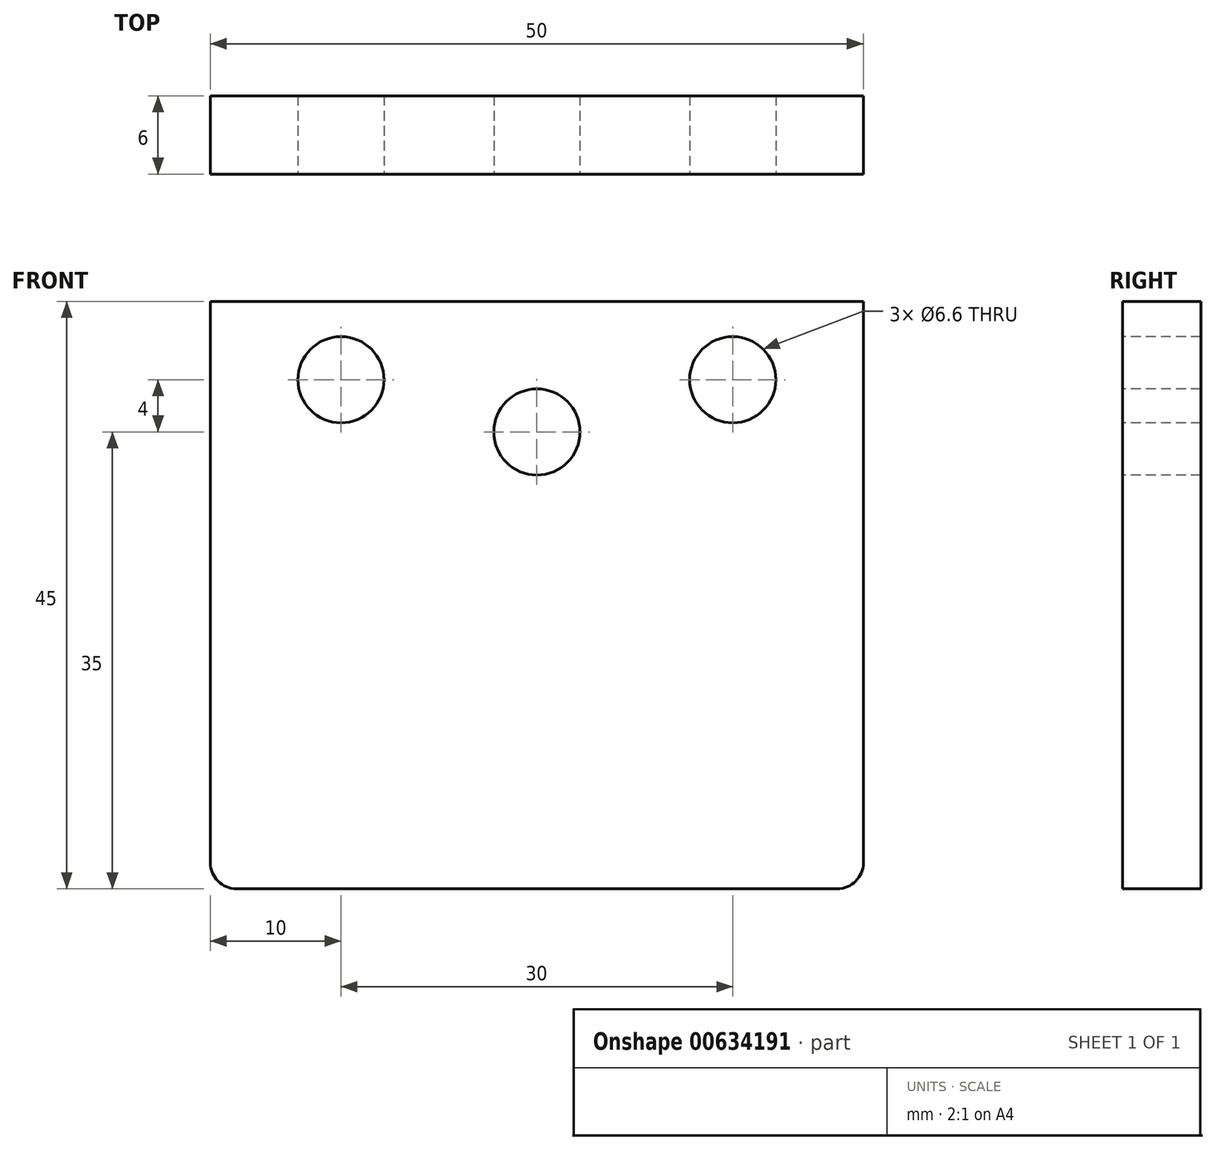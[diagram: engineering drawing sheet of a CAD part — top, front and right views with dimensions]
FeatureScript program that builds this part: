
annotation { "Feature Type Name" : "Feature", "Feature Type Description" : "" }
export const myFeature = defineFeature(function(context is Context, id is Id, definition is map)
    precondition{}
    {
        {
            var Q0;
            Q0=qCreatedBy(makeId("Front.planeOp"),FACE);
            var sketch = newSketch(context, id + "F0", { "sketchPlane" : qUnion([Q0])});
            skLineSegment(sketch, "E0.bottom", {"start": v(0, 0) * mm, "end": v(50, 0) * mm});
            skLineSegment(sketch, "E0.top", {"start": v(0, 45) * mm, "end": v(50, 45) * mm});
            skLineSegment(sketch, "E0.left", {"start": v(0, 0) * mm, "end": v(0, 45) * mm});
            skLineSegment(sketch, "E0.right", {"start": v(50, 0) * mm, "end": v(50, 45) * mm});
            skSolve(sketch);
        }
        {
            var Q0;
            Q0=makeQuery(id+"F0.imprint","IMPRINT",FACE,{"disambiguationData":[TD([[makeQuery(id+"F0.imprint","IMPRINT",EDGE,{"derivedFrom":sQuery(id+"F0.wireOp",EDGE,"E0.bottom")}),1.0]])]});
            extrude(context, id + "F1", {"entities" : qUnion([Q0]), "depth" : 6 * mm, "offsetDistance" : 25 * mm});
        }
        {
            var Q0;
            Q0=makeQuery(id+"F1.opExtrude","CAP_FACE",FACE,{"disambiguationData":[OSD([sQuery(id+"F0.wireOp",EDGE,"E0.bottom"),sQuery(id+"F0.wireOp",EDGE,"E0.top"),sQuery(id+"F0.wireOp",EDGE,"E0.left"),sQuery(id+"F0.wireOp",EDGE,"E0.right")])],"isStart":false});
            var sketch = newSketch(context, id + "F2", { "sketchPlane" : qUnion([Q0])});
            skPoint(sketch, "E1", {"position": v(10, 39) * mm});
            skPoint(sketch, "E2", {"position": v(40, 39) * mm});
            skPoint(sketch, "E3", {"position": v(25, 35) * mm});
            skPoint(sketch, "E3.positionSnap0", {"position": v(25, 45) * mm});
            skSolve(sketch);
        }
        {
            var Q0;
            Q0=sQuery(id+"F2.wireOp",VERTEX,"E1");
            var Q1;
            Q1=sQuery(id+"F2.wireOp",VERTEX,"E3");
            var Q2;
            Q2=sQuery(id+"F2.wireOp",VERTEX,"E2");
            var Q3;
            Q3=makeQuery(id+"F1.opExtrude","SWEPT_BODY",BODY,{"disambiguationData":[OSD([sQuery(id+"F0.wireOp",EDGE,"E0.bottom"),sQuery(id+"F0.wireOp",EDGE,"E0.top"),sQuery(id+"F0.wireOp",EDGE,"E0.left"),sQuery(id+"F0.wireOp",EDGE,"E0.right")])]});
            hole(context, id + "F3", {"style" : HoleStyle.SIMPLE, "endStyle" : HoleEndStyle.THROUGH, "standardTappedOrClearance" : lookupTablePath({ "standard" : "ISO", "fit" : "Normal", "size" : "M6", "type" : "Clearance" }), "standardBlindInLast" : lookupTablePath({ "fit" : "Standard", "standard" : "ISO", "size" : "M6", "type" : "Clearance" }), "holeDiameter" : 6.6 * mm, "majorDiameter" : 6 * mm, "isTappedThrough" : true, "tappedDepth" : 8 * mm, "tapClearance" : 3, "startFromSketch" : true, "locations" : qUnion([Q0, Q1, Q2]), "scope" : qUnion([Q3])});
        }
        {
            var Q0;
            Q0=makeQuery(id+"F1.opExtrude","SWEPT_EDGE",EDGE,{"disambiguationData":[OSD([sQuery(id+"F0.wireOp",EDGE,"E0.bottom"),sQuery(id+"F0.wireOp",EDGE,"E0.right")])]});
            var Q1;
            Q1=makeQuery(id+"F1.opExtrude","SWEPT_EDGE",EDGE,{"disambiguationData":[OSD([sQuery(id+"F0.wireOp",EDGE,"E0.bottom"),sQuery(id+"F0.wireOp",EDGE,"E0.left")])]});
            fillet(context, id + "F4", {"entities" : qUnion([Q0, Q1]), "radius" : 2 * mm, "tangentPropagation" : true, "allowEdgeOverflow" : false});
        }
    });
